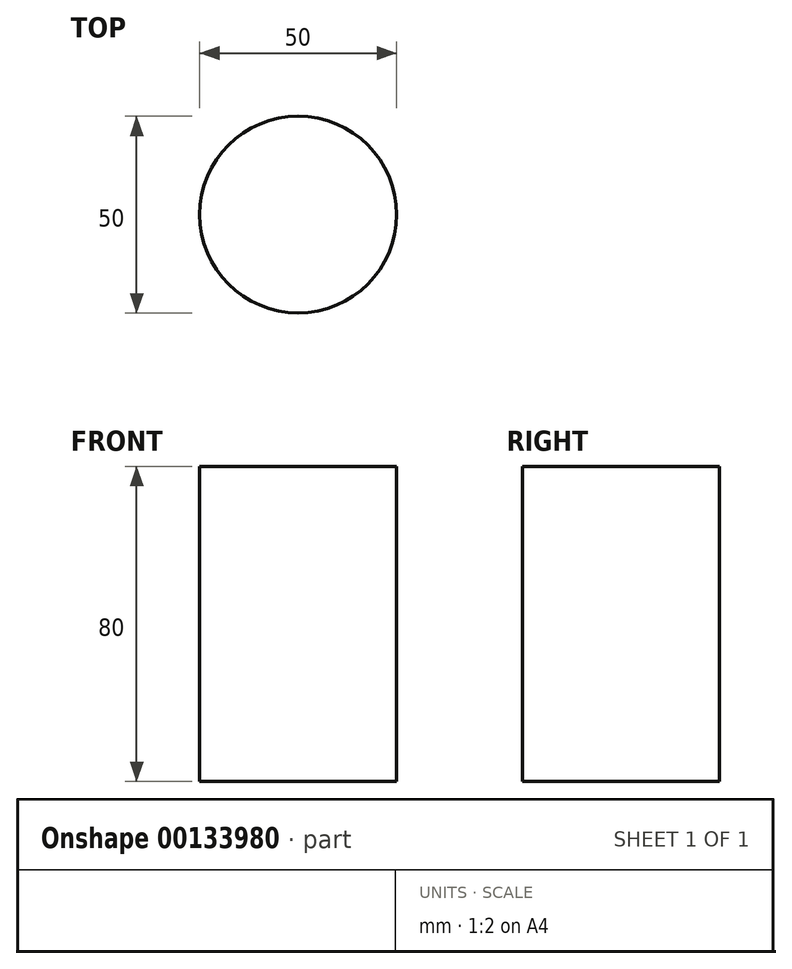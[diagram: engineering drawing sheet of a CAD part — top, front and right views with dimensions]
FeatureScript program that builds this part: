
annotation { "Feature Type Name" : "Feature", "Feature Type Description" : "" }
export const myFeature = defineFeature(function(context is Context, id is Id, definition is map)
    precondition{}
    {
        {
            var Q0;
            Q0=qCreatedBy(makeId("Top.planeOp"),FACE);
            var sketch = newSketch(context, id + "F0", { "sketchPlane" : qUnion([Q0])});
            skCircle(sketch, "E0", {"center": v(0, 0) * mm, "radius": 25 * mm});
            skSolve(sketch);
        }
        {
            var Q0;
            Q0=makeQuery(id+"F0.imprint","IMPRINT",FACE,{"disambiguationData":[TD([[makeQuery(id+"F0.imprint","IMPRINT",EDGE,{"derivedFrom":sQuery(id+"F0.wireOp",EDGE,"E0")}),1.0]])]});
            extrude(context, id + "F1", {"entities" : qUnion([Q0]), "depth" : 80 * mm, "offsetDistance" : 25 * mm});
        }
    });
